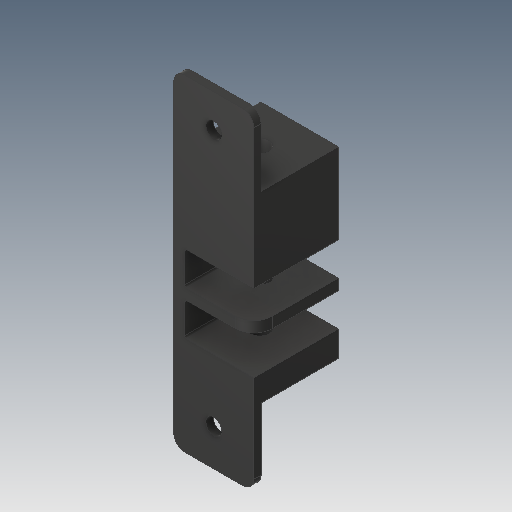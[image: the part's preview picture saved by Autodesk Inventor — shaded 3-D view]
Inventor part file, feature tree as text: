
AUTODESK INVENTOR PART (.ipt)
format: ipt  version: 2019 (Build 230136000, 136)  size: 152,064 bytes
history: native  units: mm
features: sketch x5, other x3
ambient origin geometry x8: Origin, YZ Plane, XZ Plane, XY Plane, X Axis, Y Axis, Z Axis, Center Point
bodies: Solid1 (feature_tree)
feature tree (8):
  other  "Idler Left.ipt"
  other  "Solid2::Idler Left.ipt"
  other  "TaggingFeature1"
  sketch  "Sketch3"  dims[d0=10.0mm]
  sketch  "Sketch11"
  sketch  "Sketch13"
  sketch  "Sketch14"
  sketch  "Sketch15"
